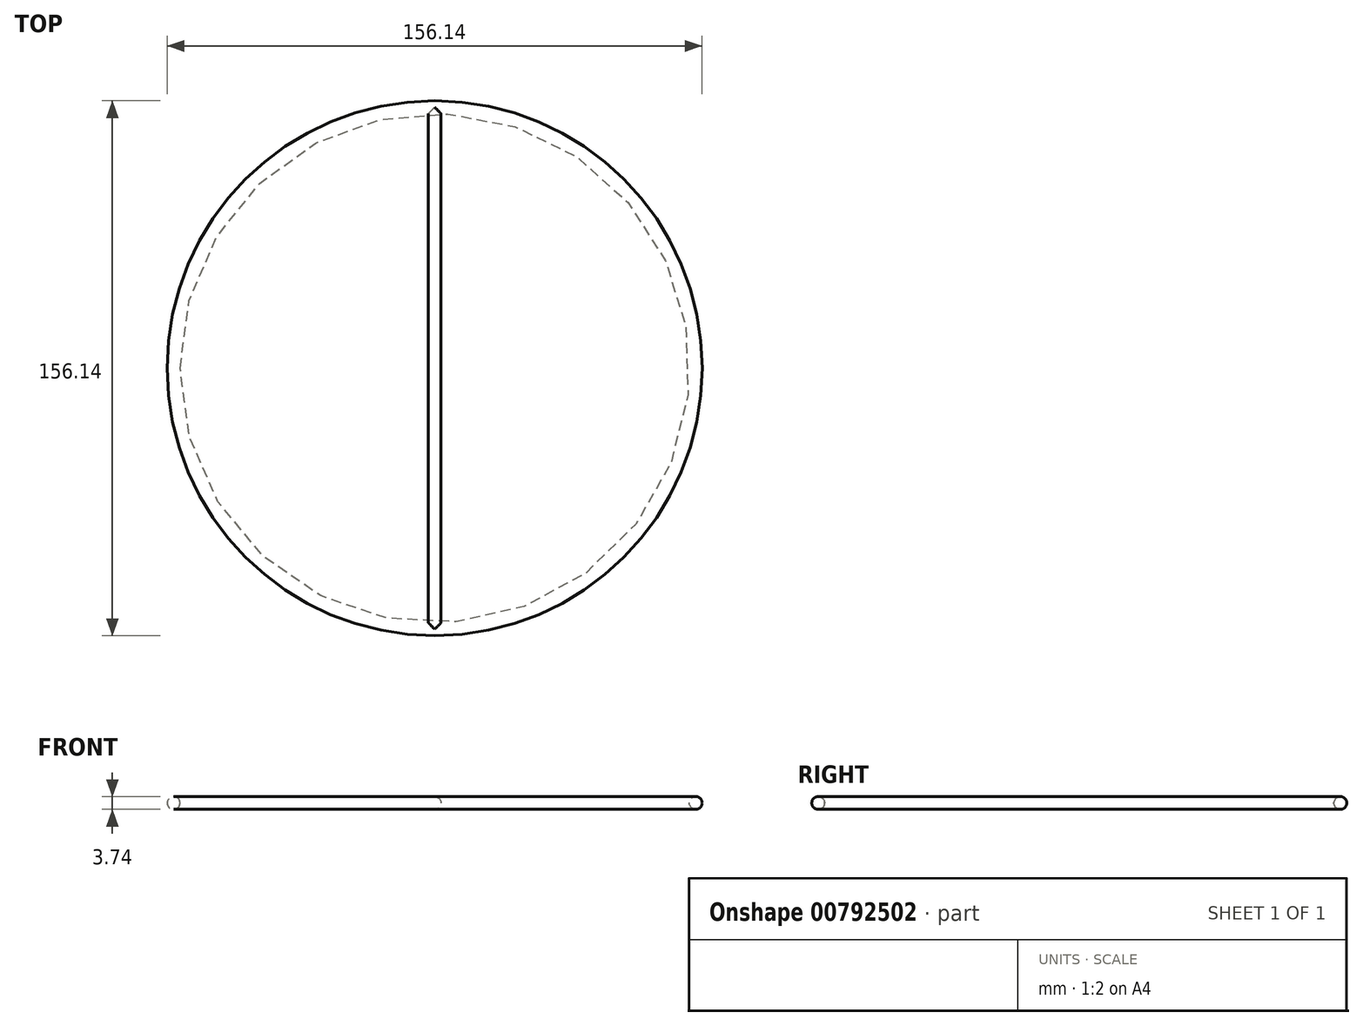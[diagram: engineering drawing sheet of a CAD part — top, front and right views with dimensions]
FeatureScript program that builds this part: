
annotation { "Feature Type Name" : "Feature", "Feature Type Description" : "" }
export const myFeature = defineFeature(function(context is Context, id is Id, definition is map)
    precondition{}
    {
        {
            var Q0;
            Q0=qCreatedBy(makeId("Front.planeOp"),FACE);
            var sketch = newSketch(context, id + "F0", { "sketchPlane" : qUnion([Q0])});
            skCircle(sketch, "E0", {"center": v(76.2, 0) * mm, "radius": 1.87 * mm});
            skCircle(sketch, "E1", {"center": v(-76.2, 0) * mm, "radius": 1.87 * mm});
            skLineSegment(sketch, "E2", {"start": v(0, 8.3) * mm, "end": v(0, -8.17) * mm});
            skLineSegment(sketch, "E3.MirrorCS", {"start": v(0, -8.3) * mm, "end": v(0, 8.17) * mm});
            skCircle(sketch, "E4", {"center": v(0, 0) * mm, "radius": 1.87 * mm});
            skLineSegment(sketch, "E5", {"start": v(0, 0) * mm, "end": v(-76.2, 0) * mm});
            skLineSegment(sketch, "E6.MirrorCS", {"start": v(0, 0) * mm, "end": v(76.2, 0) * mm});
            skSolve(sketch);
        }
        {
            var Q0;
            Q0=sQuery(id+"F0.wireOp",EDGE,"E1");
            var Q1;
            Q1=sQuery(id+"F0.wireOp",EDGE,"E0");
            var Q2;
            Q2=sQuery(id+"F0.wireOp",EDGE,"E2");
            revolve(context, id + "F1", {"bodyType" : ToolBodyType.SURFACE, "surfaceOperationType" : NewSurfaceOperationType.NEW, "surfaceEntities" : qUnion([Q0, Q1]), "axis" : qUnion([Q2]), "revolveType" : RevolveType.FULL});
        }
        {
            var Q0;
            Q0=sQuery(id+"F0.wireOp",EDGE,"E4");
            extrude(context, id + "F2", {"bodyType" : ToolBodyType.SURFACE, "surfaceEntities" : qUnion([Q0]), "endBound" : BoundingType.UP_TO_NEXT, "depth" : 127 * mm, "offsetDistance" : 25.4 * mm, "hasSecondDirection" : true, "secondDirectionBound" : SecondDirectionBoundingType.UP_TO_NEXT, "secondDirectionOppositeDirection" : true, "secondDirectionDepth" : 101.6 * mm});
        }
    });
